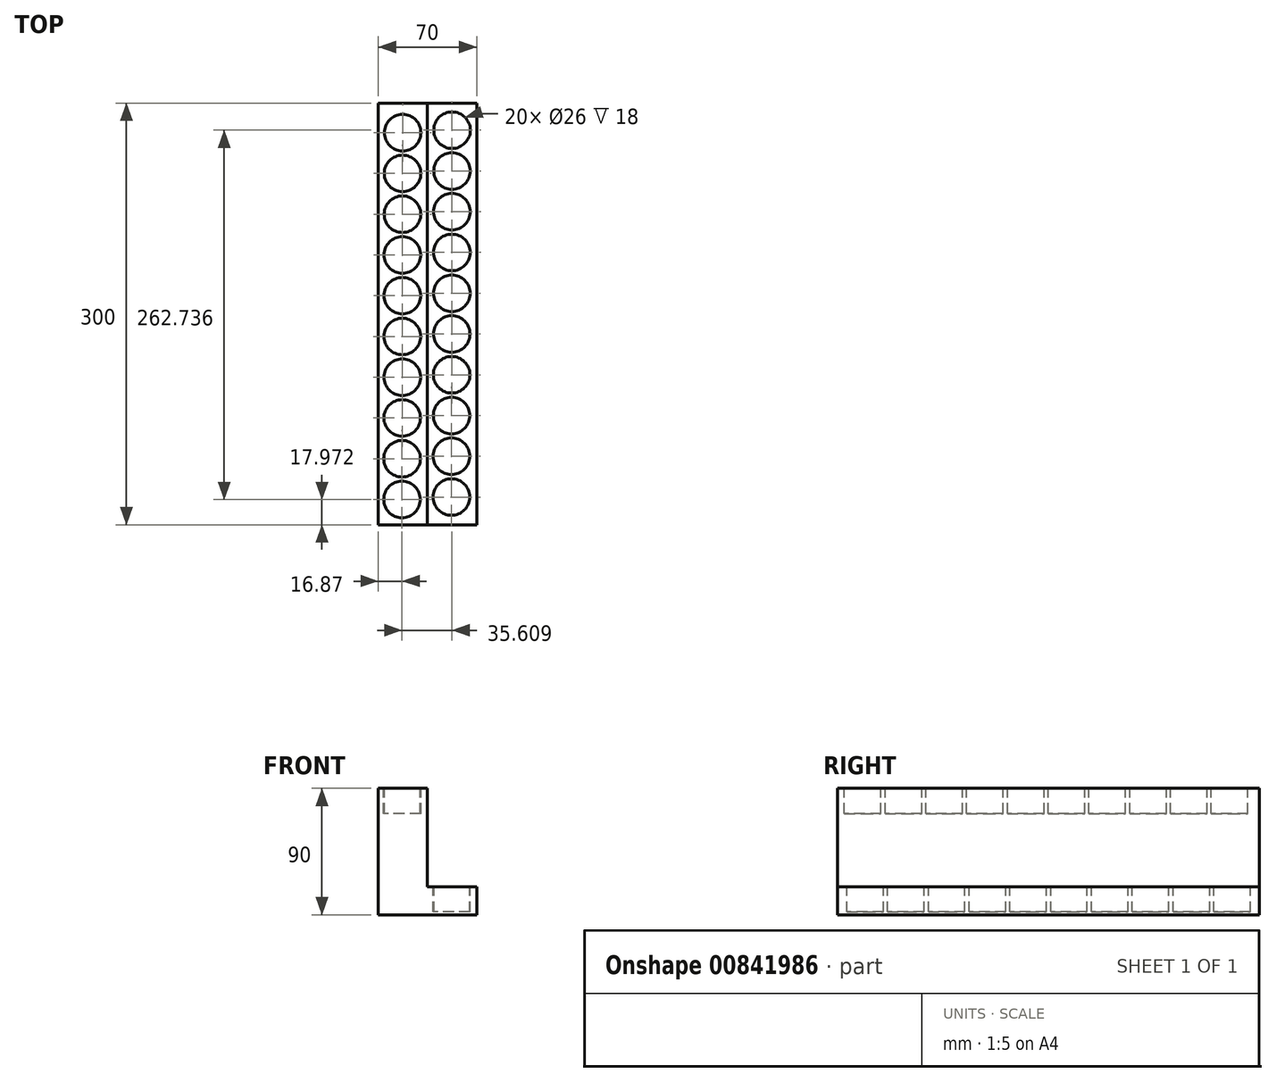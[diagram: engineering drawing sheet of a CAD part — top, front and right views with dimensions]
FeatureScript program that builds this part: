
annotation { "Feature Type Name" : "Feature", "Feature Type Description" : "" }
export const myFeature = defineFeature(function(context is Context, id is Id, definition is map)
    precondition{}
    {
        {
            var Q0;
            Q0=qCreatedBy(makeId("Front.planeOp"),FACE);
            var sketch = newSketch(context, id + "F0", { "sketchPlane" : qUnion([Q0])});
            skLineSegment(sketch, "E0", {"start": v(-49.25, 50.23) * mm, "end": v(-14.25, 50.23) * mm});
            skLineSegment(sketch, "E1", {"start": v(-14.25, 50.23) * mm, "end": v(-14.25, -19.77) * mm});
            skLineSegment(sketch, "E2", {"start": v(-14.25, -19.77) * mm, "end": v(20.75, -19.77) * mm});
            skLineSegment(sketch, "E3", {"start": v(20.75, -19.77) * mm, "end": v(20.75, -39.77) * mm});
            skLineSegment(sketch, "E4", {"start": v(-49.25, 50.23) * mm, "end": v(-49.25, -39.77) * mm});
            skLineSegment(sketch, "E5", {"start": v(-49.25, -39.77) * mm, "end": v(20.75, -39.77) * mm});
            skSolve(sketch);
        }
        {
            var Q0;
            Q0 = qSketchRegion(id + "F0", true);
            extrude(context, id + "F1", {"entities" : qUnion([Q0]), "depth" : 300 * mm, "offsetDistance" : 25 * mm});
        }
        {
            var Q0;
            Q0=makeQuery(id+"F1.opExtrude","SWEPT_FACE",FACE,{"disambiguationData":[OSD([sQuery(id+"F0.wireOp",EDGE,"E2")])]});
            var sketch = newSketch(context, id + "F2", { "sketchPlane" : qUnion([Q0])});
            skCircle(sketch, "E6", {"center": v(2.79, -280.3) * mm, "radius": 13 * mm});
            skLineSegment(sketch, "E7.direction1", {"start": v(2.79, -280.3) * mm, "end": v(2.5, -251.3) * mm, "construction": true});
            skCircle(sketch, "E8.1.0.0", {"center": v(2.83, -251.3) * mm, "radius": 13 * mm});
            skCircle(sketch, "E8.2.0.0", {"center": v(2.88, -222.3) * mm, "radius": 13 * mm});
            skCircle(sketch, "E8.3.0.0", {"center": v(2.93, -193.3) * mm, "radius": 13 * mm});
            skCircle(sketch, "E8.4.0.0", {"center": v(2.98, -164.3) * mm, "radius": 13 * mm});
            skCircle(sketch, "E8.5.0.0", {"center": v(3.03, -135.3) * mm, "radius": 13 * mm});
            skCircle(sketch, "E8.6.0.0", {"center": v(3.08, -106.3) * mm, "radius": 13 * mm});
            skCircle(sketch, "E8.7.0.0", {"center": v(3.13, -77.3) * mm, "radius": 13 * mm});
            skCircle(sketch, "E8.8.0.0", {"center": v(3.18, -48.3) * mm, "radius": 13 * mm});
            skCircle(sketch, "E8.9.0.0", {"center": v(3.23, -19.3) * mm, "radius": 13 * mm});
            skLineSegment(sketch, "E8.direction1", {"start": v(2.79, -280.3) * mm, "end": v(2.83, -251.3) * mm, "construction": true});
            skSolve(sketch);
        }
        {
            var Q0;
            Q0=makeQuery(id+"F1.opExtrude","SWEPT_FACE",FACE,{"disambiguationData":[OSD([sQuery(id+"F0.wireOp",EDGE,"E0")])]});
            var sketch = newSketch(context, id + "F3", { "sketchPlane" : qUnion([Q0])});
            skCircle(sketch, "E9", {"center": v(-32.38, -282.03) * mm, "radius": 13 * mm});
            skLineSegment(sketch, "E10.direction1", {"start": v(-32.38, -282.03) * mm, "end": v(-32.67, -253.03) * mm, "construction": true});
            skCircle(sketch, "E11.1.0.0", {"center": v(-32.33, -253.03) * mm, "radius": 13 * mm});
            skCircle(sketch, "E11.2.0.0", {"center": v(-32.28, -224.03) * mm, "radius": 13 * mm});
            skCircle(sketch, "E11.3.0.0", {"center": v(-32.23, -195.03) * mm, "radius": 13 * mm});
            skCircle(sketch, "E11.4.0.0", {"center": v(-32.18, -166.03) * mm, "radius": 13 * mm});
            skCircle(sketch, "E11.5.0.0", {"center": v(-32.13, -137.03) * mm, "radius": 13 * mm});
            skCircle(sketch, "E11.6.0.0", {"center": v(-32.08, -108.03) * mm, "radius": 13 * mm});
            skCircle(sketch, "E11.7.0.0", {"center": v(-32.04, -79.03) * mm, "radius": 13 * mm});
            skCircle(sketch, "E11.8.0.0", {"center": v(-31.99, -50.03) * mm, "radius": 13 * mm});
            skCircle(sketch, "E11.9.0.0", {"center": v(-31.94, -21.03) * mm, "radius": 13 * mm});
            skLineSegment(sketch, "E11.direction1", {"start": v(-32.38, -282.03) * mm, "end": v(-32.33, -253.03) * mm, "construction": true});
            skSolve(sketch);
        }
        {
            var Q0;
            Q0 = qSketchRegion(id + "F2", true);
            extrude(context, id + "F4", {"entities" : qUnion([Q0]), "operationType" : NewBodyOperationType.REMOVE, "oppositeDirection" : true, "depth" : 18 * mm, "offsetDistance" : 25 * mm});
        }
        {
            var Q0;
            Q0 = qSketchRegion(id + "F3", true);
            extrude(context, id + "F5", {"entities" : qUnion([Q0]), "operationType" : NewBodyOperationType.REMOVE, "oppositeDirection" : true, "depth" : 18 * mm, "offsetDistance" : 25 * mm});
        }
    });
